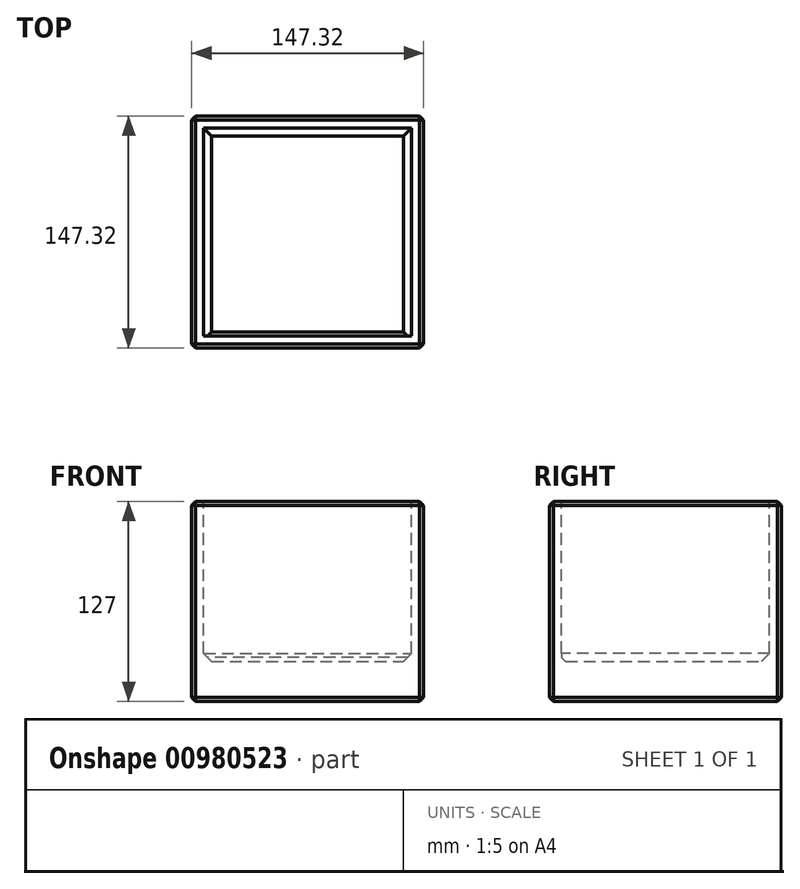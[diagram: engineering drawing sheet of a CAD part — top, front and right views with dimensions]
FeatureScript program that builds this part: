
annotation { "Feature Type Name" : "Feature", "Feature Type Description" : "" }
export const myFeature = defineFeature(function(context is Context, id is Id, definition is map)
    precondition{}
    {
        {
            var Q0;
            Q0=qCreatedBy(makeId("Top.planeOp"),FACE);
            var sketch = newSketch(context, id + "F0", { "sketchPlane" : qUnion([Q0])});
            skLineSegment(sketch, "E0.bottom", {"start": v(73.66, -73.66) * mm, "end": v(-73.66, -73.66) * mm});
            skLineSegment(sketch, "E0.top", {"start": v(73.66, 73.66) * mm, "end": v(-73.66, 73.66) * mm});
            skLineSegment(sketch, "E0.left", {"start": v(73.66, -73.66) * mm, "end": v(73.66, 73.66) * mm});
            skLineSegment(sketch, "E0.right", {"start": v(-73.66, -73.66) * mm, "end": v(-73.66, 73.66) * mm});
            skPoint(sketch, "E0.middle", {"position": v(0, 0) * mm});
            skLineSegment(sketch, "E1.bottom", {"start": v(60.96, 60.96) * mm, "end": v(-60.96, 60.96) * mm});
            skLineSegment(sketch, "E1.top", {"start": v(60.96, -60.96) * mm, "end": v(-60.96, -60.96) * mm});
            skLineSegment(sketch, "E1.left", {"start": v(-60.96, -60.96) * mm, "end": v(-60.96, 60.96) * mm});
            skLineSegment(sketch, "E1.right", {"start": v(60.96, -60.96) * mm, "end": v(60.96, 60.96) * mm});
            skSolve(sketch);
        }
        {
            var Q0;
            Q0=makeQuery(id+"F0.imprint","IMPRINT",FACE,{"disambiguationData":[TD([[makeQuery(id+"F0.imprint","IMPRINT",EDGE,{"derivedFrom":sQuery(id+"F0.wireOp",EDGE,"E0.bottom")}),-1.0]])]});
            var Q1;
            Q1=makeQuery(id+"F0.imprint","IMPRINT",FACE,{"disambiguationData":[TD([[makeQuery(id+"F0.imprint","IMPRINT",EDGE,{"derivedFrom":sQuery(id+"F0.wireOp",EDGE,"E1.bottom")}),1.0]])]});
            extrude(context, id + "F1", {"entities" : qUnion([Q0, Q1]), "endBound" : BoundingType.SYMMETRIC, "depth" : 127 * mm, "offsetDistance" : 25.4 * mm});
        }
        {
            var Q0;
            Q0=makeQuery(id+"F1.opExtrude","CAP_FACE",FACE,{"disambiguationData":[OSD([sQuery(id+"F0.wireOp",EDGE,"E0.bottom"),sQuery(id+"F0.wireOp",EDGE,"E0.top"),sQuery(id+"F0.wireOp",EDGE,"E0.left"),sQuery(id+"F0.wireOp",EDGE,"E0.right")])],"isStart":false});
            var sketch = newSketch(context, id + "F2", { "sketchPlane" : qUnion([Q0])});
            skLineSegment(sketch, "E2.bottom", {"start": v(66.04, 66.04) * mm, "end": v(-66.04, 66.04) * mm});
            skLineSegment(sketch, "E2.top", {"start": v(66.04, -66.04) * mm, "end": v(-66.04, -66.04) * mm});
            skLineSegment(sketch, "E2.left", {"start": v(66.04, -66.04) * mm, "end": v(66.04, 66.04) * mm});
            skLineSegment(sketch, "E2.right", {"start": v(-66.04, -66.04) * mm, "end": v(-66.04, 66.04) * mm});
            skPoint(sketch, "E2.middle", {"position": v(0, 0) * mm});
            skSolve(sketch);
        }
        {
            var Q0;
            Q0=makeQuery(id+"F2.imprint","IMPRINT",FACE,{"disambiguationData":[TD([[makeQuery(id+"F2.imprint","IMPRINT",EDGE,{"derivedFrom":sQuery(id+"F2.wireOp",EDGE,"E2.bottom")}),1.0]])]});
            extrude(context, id + "F3", {"entities" : qUnion([Q0]), "operationType" : NewBodyOperationType.REMOVE, "oppositeDirection" : true, "depth" : 101.6 * mm, "offsetDistance" : 25.4 * mm});
        }
        {
            var Q0;
            Q0=makeQuery(id+"F1.opExtrude","SWEPT_EDGE",EDGE,{"disambiguationData":[OSD([sQuery(id+"F0.wireOp",EDGE,"E0.bottom"),sQuery(id+"F0.wireOp",EDGE,"E0.right")])]});
            var Q1;
            Q1=makeQuery(id+"F1.opExtrude","CAP_EDGE",EDGE,{"disambiguationData":[OSD([sQuery(id+"F0.wireOp",EDGE,"E0.right")])],"isStart":false});
            var Q2;
            Q2=makeQuery(id+"F1.opExtrude","SWEPT_EDGE",EDGE,{"disambiguationData":[OSD([sQuery(id+"F0.wireOp",EDGE,"E0.top"),sQuery(id+"F0.wireOp",EDGE,"E0.right")])]});
            var Q3;
            Q3=makeQuery(id+"F1.opExtrude","CAP_EDGE",EDGE,{"disambiguationData":[OSD([sQuery(id+"F0.wireOp",EDGE,"E0.right")])],"isStart":true});
            var Q4;
            Q4=makeQuery(id+"F1.opExtrude","CAP_EDGE",EDGE,{"disambiguationData":[OSD([sQuery(id+"F0.wireOp",EDGE,"E0.bottom")])],"isStart":false});
            var Q5;
            Q5=makeQuery(id+"F1.opExtrude","SWEPT_EDGE",EDGE,{"disambiguationData":[OSD([sQuery(id+"F0.wireOp",EDGE,"E0.bottom"),sQuery(id+"F0.wireOp",EDGE,"E0.left")])]});
            var Q6;
            Q6=makeQuery(id+"F1.opExtrude","CAP_EDGE",EDGE,{"disambiguationData":[OSD([sQuery(id+"F0.wireOp",EDGE,"E0.bottom")])],"isStart":true});
            var Q7;
            Q7=makeQuery(id+"F3.boolean.opBoolean","COPY",EDGE,{"derivedFrom":makeQuery(id+"F3.opExtrude","CAP_EDGE",EDGE,{"disambiguationData":[OSD([sQuery(id+"F2.wireOp",EDGE,"E2.left")])],"isStart":true})});
            var Q8;
            Q8=makeQuery(id+"F3.boolean.opBoolean","COPY",EDGE,{"derivedFrom":makeQuery(id+"F3.opExtrude","CAP_EDGE",EDGE,{"disambiguationData":[OSD([sQuery(id+"F2.wireOp",EDGE,"E2.top")])],"isStart":true})});
            var Q9;
            Q9=makeQuery(id+"F1.opExtrude","CAP_EDGE",EDGE,{"disambiguationData":[OSD([sQuery(id+"F0.wireOp",EDGE,"E0.left")])],"isStart":false});
            var Q10;
            Q10=makeQuery(id+"F1.opExtrude","CAP_EDGE",EDGE,{"disambiguationData":[OSD([sQuery(id+"F0.wireOp",EDGE,"E0.left")])],"isStart":true});
            var Q11;
            Q11=makeQuery(id+"F1.opExtrude","SWEPT_EDGE",EDGE,{"disambiguationData":[OSD([sQuery(id+"F0.wireOp",EDGE,"E0.top"),sQuery(id+"F0.wireOp",EDGE,"E0.left")])]});
            var Q12;
            Q12=makeQuery(id+"F1.opExtrude","CAP_EDGE",EDGE,{"disambiguationData":[OSD([sQuery(id+"F0.wireOp",EDGE,"E0.top")])],"isStart":false});
            var Q13;
            Q13=makeQuery(id+"F1.opExtrude","CAP_EDGE",EDGE,{"disambiguationData":[OSD([sQuery(id+"F0.wireOp",EDGE,"E0.top")])],"isStart":true});
            var Q14;
            Q14=makeQuery(id+"F3.boolean.opBoolean","COPY",EDGE,{"derivedFrom":makeQuery(id+"F3.opExtrude","CAP_EDGE",EDGE,{"disambiguationData":[OSD([sQuery(id+"F2.wireOp",EDGE,"E2.right")])],"isStart":true})});
            var Q15;
            Q15=makeQuery(id+"F3.boolean.opBoolean","COPY",EDGE,{"derivedFrom":makeQuery(id+"F3.opExtrude","CAP_EDGE",EDGE,{"disambiguationData":[OSD([sQuery(id+"F2.wireOp",EDGE,"E2.bottom")])],"isStart":true})});
            var Q16;
            Q16=makeQuery(id+"F3.boolean.opBoolean","COPY",EDGE,{"derivedFrom":makeQuery(id+"F3.opExtrude","CAP_EDGE",EDGE,{"disambiguationData":[OSD([sQuery(id+"F2.wireOp",EDGE,"E2.top")])],"isStart":false})});
            chamfer(context, id + "F4", {"entities" : qUnion([Q0, Q1, Q2, Q3, Q4, Q5, Q6, Q7, Q8, Q9, Q10, Q11, Q12, Q13, Q14, Q15, Q16]), "width" : 2.54 * mm, "tangentPropagation" : true});
        }
        {
            var Q0;
            Q0=makeQuery(id+"F3.boolean.opBoolean","COPY",EDGE,{"derivedFrom":makeQuery(id+"F3.opExtrude","CAP_EDGE",EDGE,{"disambiguationData":[OSD([sQuery(id+"F2.wireOp",EDGE,"E2.left")])],"isStart":false})});
            var Q1;
            Q1=makeQuery(id+"F3.boolean.opBoolean","COPY",EDGE,{"derivedFrom":makeQuery(id+"F3.opExtrude","CAP_EDGE",EDGE,{"disambiguationData":[OSD([sQuery(id+"F2.wireOp",EDGE,"E2.bottom")])],"isStart":false})});
            var Q2;
            Q2=makeQuery(id+"F3.boolean.opBoolean","COPY",EDGE,{"derivedFrom":makeQuery(id+"F3.opExtrude","CAP_EDGE",EDGE,{"disambiguationData":[OSD([sQuery(id+"F2.wireOp",EDGE,"E2.right")])],"isStart":false})});
            chamfer(context, id + "F5", {"entities" : qUnion([Q0, Q1, Q2]), "width" : 5.08 * mm, "tangentPropagation" : true});
        }
    });
